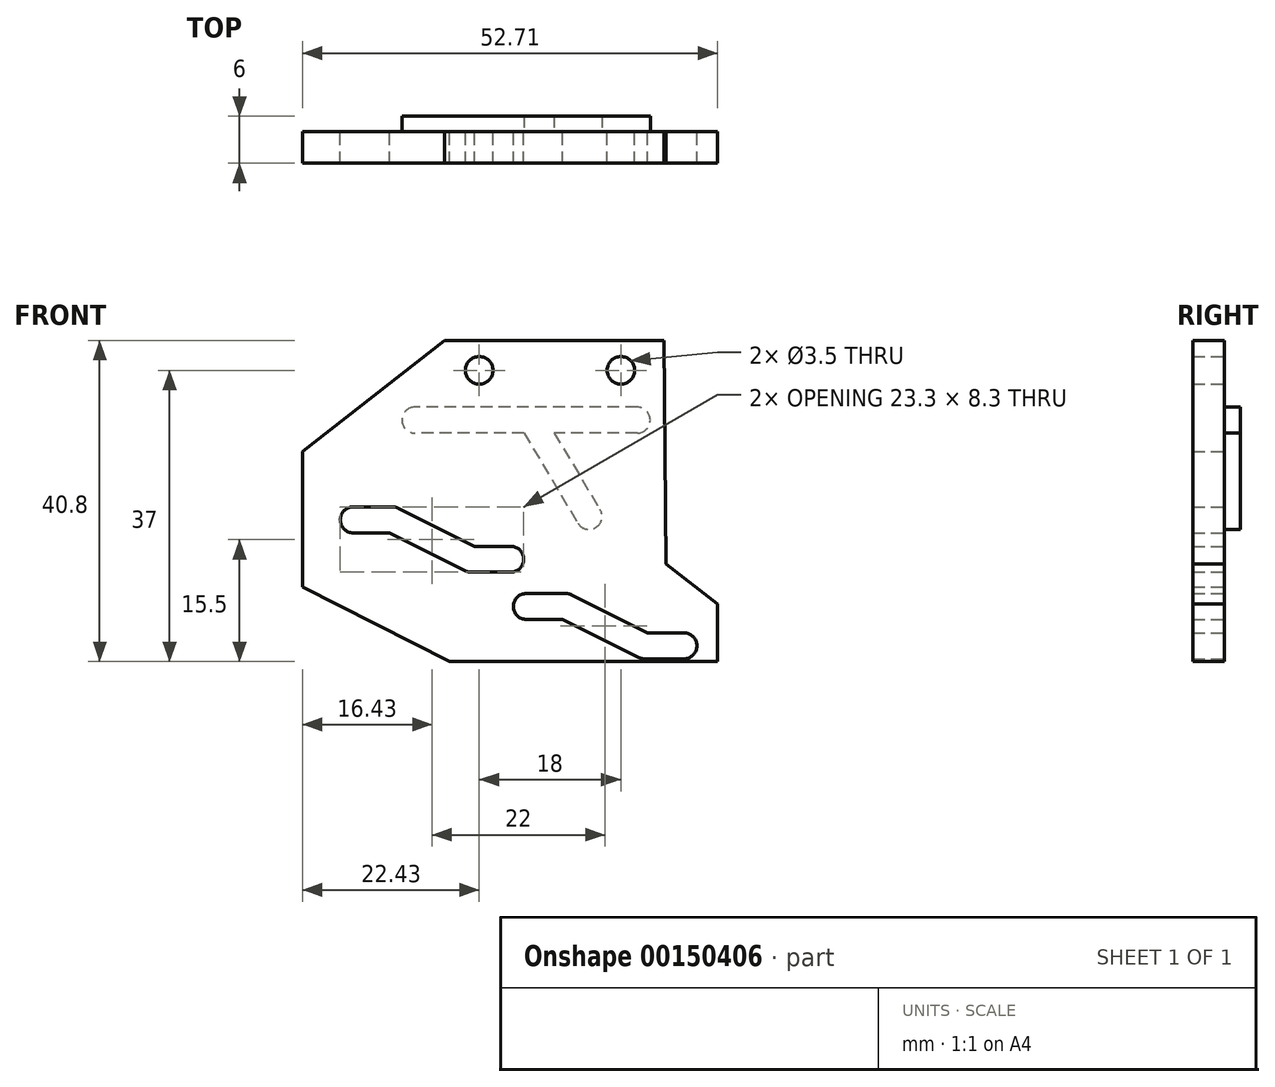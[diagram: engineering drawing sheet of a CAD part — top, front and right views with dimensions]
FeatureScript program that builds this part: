
annotation { "Feature Type Name" : "Feature", "Feature Type Description" : "" }
export const myFeature = defineFeature(function(context is Context, id is Id, definition is map)
    precondition{}
    {
        {
            var Q0;
            Q0=qCreatedBy(makeId("Front.planeOp"),FACE);
            var sketch = newSketch(context, id + "F0", { "sketchPlane" : qUnion([Q0])});
            skCircle(sketch, "E0", {"center": v(-9, 45) * mm, "radius": 1.75 * mm});
            skCircle(sketch, "E1", {"center": v(9, 45) * mm, "radius": 1.75 * mm});
            skLineSegment(sketch, "E2", {"start": v(-9, 45) * mm, "end": v(9, 45) * mm, "construction": true});
            skLineSegment(sketch, "E3", {"start": v(0, 45) * mm, "end": v(0, 0) * mm, "construction": true});
            skLineSegment(sketch, "E4", {"start": v(5.27, 10) * mm, "end": v(-14.09, 10) * mm, "construction": true});
            skCircle(sketch, "E5", {"center": v(12, 10) * mm, "radius": 1.55 * mm, "construction": true});
            skCircle(sketch, "E6", {"center": v(-10, 21) * mm, "radius": 1.55 * mm, "construction": true});
            skLineSegment(sketch, "E7", {"start": v(-10, 21) * mm, "end": v(12, 10) * mm, "construction": true});
            skSolve(sketch);
        }
        {
            var Q0;
            Q0=qCreatedBy(makeId("Front.planeOp"),FACE);
            var sketch = newSketch(context, id + "F1", { "sketchPlane" : qUnion([Q0])});
            skLineSegment(sketch, "E8", {"start": v(12, 10) * mm, "end": v(17, 10) * mm});
            skLineSegment(sketch, "E9", {"start": v(12, 10) * mm, "end": v(2, 15) * mm});
            skLineSegment(sketch, "E10", {"start": v(2, 15) * mm, "end": v(-3, 15) * mm});
            skArc(sketch, "E11.0.startCap", {"start": v(12.74, 11.48) * mm, "mid": v(13.48, 9.26) * mm, "end": v(11.26, 8.52) * mm});
            skArc(sketch, "E11.0.endCap", {"start": v(1.26, 13.52) * mm, "mid": v(0.52, 15.74) * mm, "end": v(2.74, 16.48) * mm});
            skLineSegment(sketch, "E11.0.left", {"start": v(11.26, 8.52) * mm, "end": v(1.26, 13.52) * mm});
            skLineSegment(sketch, "E11.0.right", {"start": v(12.74, 11.48) * mm, "end": v(2.74, 16.48) * mm});
            skArc(sketch, "E11.1.startCap", {"start": v(2, 16.65) * mm, "mid": v(3.65, 15) * mm, "end": v(2, 13.35) * mm});
            skArc(sketch, "E11.1.endCap", {"start": v(-3, 13.35) * mm, "mid": v(-4.65, 15) * mm, "end": v(-3, 16.65) * mm});
            skLineSegment(sketch, "E11.1.left", {"start": v(2, 13.35) * mm, "end": v(-3, 13.35) * mm});
            skLineSegment(sketch, "E11.1.right", {"start": v(2, 16.65) * mm, "end": v(-3, 16.65) * mm});
            skArc(sketch, "E11.2.startCap", {"start": v(12, 8.35) * mm, "mid": v(10.35, 10) * mm, "end": v(12, 11.65) * mm});
            skArc(sketch, "E11.2.endCap", {"start": v(17, 11.65) * mm, "mid": v(18.65, 10) * mm, "end": v(17, 8.35) * mm});
            skLineSegment(sketch, "E11.2.left", {"start": v(12, 11.65) * mm, "end": v(17, 11.65) * mm});
            skLineSegment(sketch, "E11.2.right", {"start": v(12, 8.35) * mm, "end": v(17, 8.35) * mm});
            skSolve(sketch);
        }
        {
            var Q0;
            Q0=qCreatedBy(makeId("Front.planeOp"),FACE);
            var sketch = newSketch(context, id + "F2", { "sketchPlane" : qUnion([Q0])});
            skLineSegment(sketch, "E12", {"start": v(-10, 21) * mm, "end": v(-5, 21) * mm});
            skLineSegment(sketch, "E13", {"start": v(-10, 21) * mm, "end": v(-20, 26) * mm});
            skLineSegment(sketch, "E14", {"start": v(-20, 26) * mm, "end": v(-25, 26) * mm});
            skArc(sketch, "E15.0.startCap", {"start": v(-9.26, 22.48) * mm, "mid": v(-8.52, 20.26) * mm, "end": v(-10.74, 19.52) * mm});
            skArc(sketch, "E15.0.endCap", {"start": v(-20.74, 24.52) * mm, "mid": v(-21.48, 26.74) * mm, "end": v(-19.26, 27.48) * mm});
            skLineSegment(sketch, "E15.0.left", {"start": v(-10.74, 19.52) * mm, "end": v(-20.74, 24.52) * mm});
            skLineSegment(sketch, "E15.0.right", {"start": v(-9.26, 22.48) * mm, "end": v(-19.26, 27.48) * mm});
            skArc(sketch, "E15.1.startCap", {"start": v(-20, 27.65) * mm, "mid": v(-18.35, 26) * mm, "end": v(-20, 24.35) * mm});
            skArc(sketch, "E15.1.endCap", {"start": v(-25, 24.35) * mm, "mid": v(-26.65, 26) * mm, "end": v(-25, 27.65) * mm});
            skLineSegment(sketch, "E15.1.left", {"start": v(-20, 24.35) * mm, "end": v(-25, 24.35) * mm});
            skLineSegment(sketch, "E15.1.right", {"start": v(-20, 27.65) * mm, "end": v(-25, 27.65) * mm});
            skArc(sketch, "E15.2.startCap", {"start": v(-10, 19.35) * mm, "mid": v(-11.65, 21) * mm, "end": v(-10, 22.65) * mm});
            skArc(sketch, "E15.2.endCap", {"start": v(-5, 22.65) * mm, "mid": v(-3.35, 21) * mm, "end": v(-5, 19.35) * mm});
            skLineSegment(sketch, "E15.2.left", {"start": v(-10, 22.65) * mm, "end": v(-5, 22.65) * mm});
            skLineSegment(sketch, "E15.2.right", {"start": v(-10, 19.35) * mm, "end": v(-5, 19.35) * mm});
            skSolve(sketch);
        }
        {
            var Q0;
            Q0=qCreatedBy(makeId("Front.planeOp"),FACE);
            var sketch = newSketch(context, id + "F3", { "sketchPlane" : qUnion([Q0])});
            skLineSegment(sketch, "E16", {"start": v(14.46, 48.8) * mm, "end": v(-13.4, 48.8) * mm});
            skLineSegment(sketch, "E17", {"start": v(-13.4, 48.8) * mm, "end": v(-31.43, 34.69) * mm});
            skLineSegment(sketch, "E18", {"start": v(-31.43, 34.69) * mm, "end": v(-31.43, 17.5) * mm});
            skLineSegment(sketch, "E19", {"start": v(-31.43, 17.5) * mm, "end": v(-12.8, 8) * mm});
            skLineSegment(sketch, "E20", {"start": v(-12.8, 8) * mm, "end": v(21.28, 8) * mm});
            skLineSegment(sketch, "E21", {"start": v(21.28, 8) * mm, "end": v(21.28, 15.35) * mm});
            skLineSegment(sketch, "E22", {"start": v(21.28, 15.35) * mm, "end": v(14.7, 20.4) * mm});
            skLineSegment(sketch, "E23", {"start": v(14.7, 20.4) * mm, "end": v(14.46, 48.8) * mm});
            skSolve(sketch);
        }
        {
            var Q0;
            Q0 = qSketchRegion(id + "F3", true);
            extrude(context, id + "F4", {"entities" : qUnion([Q0]), "depth" : 4 * mm});
        }
        {
            var Q0;
            Q0 = qSketchRegion(id + "F0", true);
            var Q1;
            Q1 = qSketchRegion(id + "F1", true);
            var Q2;
            Q2 = qSketchRegion(id + "F2", true);
            extrude(context, id + "F5", {"entities" : qUnion([Q0, Q1, Q2]), "operationType" : NewBodyOperationType.REMOVE, "depth" : 25 * mm});
        }
        {
            var Q0;
            Q0=makeQuery(id+"F4.opExtrude","CAP_FACE",FACE,{"disambiguationData":[OSD([sQuery(id+"F3.wireOp",EDGE,"E16"),sQuery(id+"F3.wireOp",EDGE,"E17"),sQuery(id+"F3.wireOp",EDGE,"E18"),sQuery(id+"F3.wireOp",EDGE,"E19"),sQuery(id+"F3.wireOp",EDGE,"E20"),sQuery(id+"F3.wireOp",EDGE,"E21"),sQuery(id+"F3.wireOp",EDGE,"E22"),sQuery(id+"F3.wireOp",EDGE,"E23")])],"isStart":true});
            var sketch = newSketch(context, id + "F6", { "sketchPlane" : qUnion([Q0])});
            skLineSegment(sketch, "E24", {"start": v(-11.08, 38.68) * mm, "end": v(17.17, 38.68) * mm});
            skLineSegment(sketch, "E25", {"start": v(2.39, 38.68) * mm, "end": v(-4.95, 26.44) * mm});
            skArc(sketch, "E26.0.startCap", {"start": v(0.97, 39.53) * mm, "mid": v(3.24, 40.1) * mm, "end": v(3.8, 37.83) * mm});
            skArc(sketch, "E26.0.endCap", {"start": v(-3.54, 25.6) * mm, "mid": v(-5.8, 25.02) * mm, "end": v(-6.37, 27.29) * mm});
            skLineSegment(sketch, "E26.0.left", {"start": v(3.8, 37.83) * mm, "end": v(-3.54, 25.6) * mm});
            skLineSegment(sketch, "E26.0.right", {"start": v(0.97, 39.53) * mm, "end": v(-6.37, 27.29) * mm});
            skArc(sketch, "E26.1.startCap", {"start": v(-11.08, 37.03) * mm, "mid": v(-12.73, 38.68) * mm, "end": v(-11.08, 40.33) * mm});
            skArc(sketch, "E26.1.endCap", {"start": v(17.17, 40.33) * mm, "mid": v(18.82, 38.68) * mm, "end": v(17.17, 37.03) * mm});
            skLineSegment(sketch, "E26.1.left", {"start": v(-11.08, 40.33) * mm, "end": v(17.17, 40.33) * mm});
            skLineSegment(sketch, "E26.1.right", {"start": v(-11.08, 37.03) * mm, "end": v(17.17, 37.03) * mm});
            skSolve(sketch);
        }
        {
            var Q0;
            Q0 = qSketchRegion(id + "F6", true);
            extrude(context, id + "F7", {"entities" : qUnion([Q0]), "operationType" : NewBodyOperationType.ADD, "depth" : 2 * mm});
        }
    });
